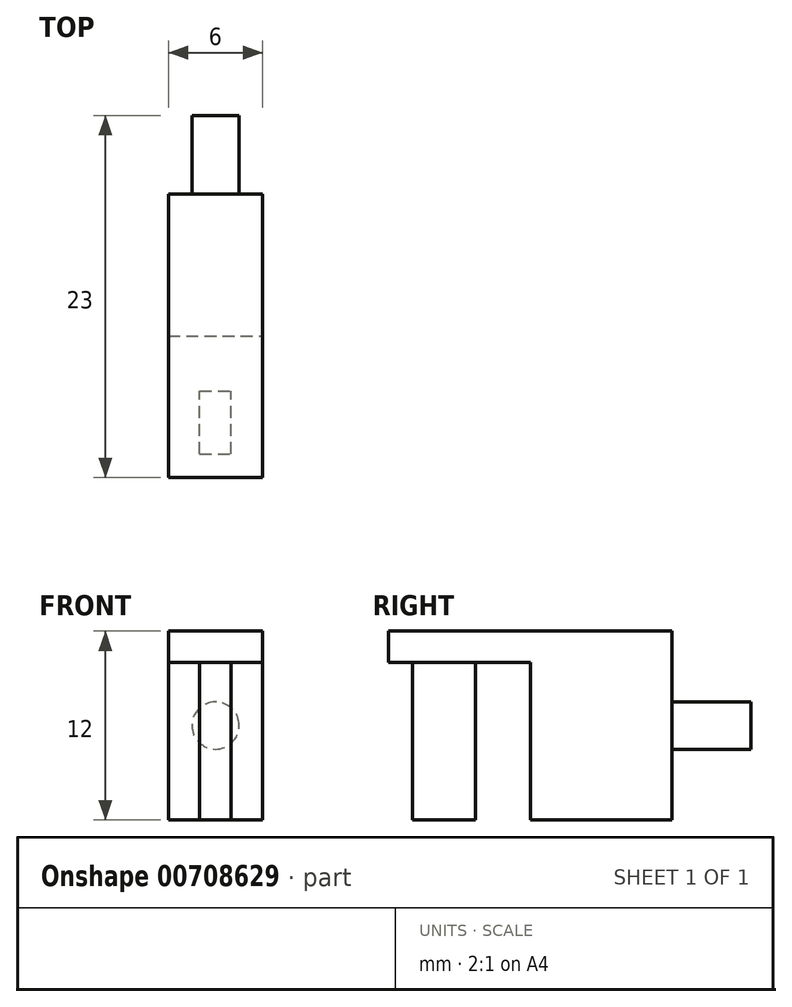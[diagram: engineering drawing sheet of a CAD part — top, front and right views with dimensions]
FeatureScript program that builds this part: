
annotation { "Feature Type Name" : "Feature", "Feature Type Description" : "" }
export const myFeature = defineFeature(function(context is Context, id is Id, definition is map)
    precondition{}
    {
        {
            var Q0;
            Q0=qCreatedBy(makeId("Top.planeOp"),FACE);
            var sketch = newSketch(context, id + "F0", { "sketchPlane" : qUnion([Q0])});
            skLineSegment(sketch, "E0.bottom", {"start": v(-3, 9) * mm, "end": v(3, 9) * mm});
            skLineSegment(sketch, "E0.top", {"start": v(-3, -9) * mm, "end": v(3, -9) * mm});
            skLineSegment(sketch, "E0.left", {"start": v(-3, 9) * mm, "end": v(-3, -9) * mm});
            skLineSegment(sketch, "E0.right", {"start": v(3, 9) * mm, "end": v(3, -9) * mm});
            skPoint(sketch, "E0.middle", {"position": v(0, 0) * mm});
            skSolve(sketch);
        }
        {
            var Q0;
            Q0=makeQuery(id+"F0.imprint","IMPRINT",FACE,{"disambiguationData":[TD([[makeQuery(id+"F0.imprint","IMPRINT",EDGE,{"derivedFrom":sQuery(id+"F0.wireOp",EDGE,"E0.bottom")}),-1.0]])]});
            extrude(context, id + "F1", {"entities" : qUnion([Q0]), "depth" : 12 * mm, "offsetDistance" : 25 * mm});
        }
        {
            var Q0;
            Q0=makeQuery(id+"F1.opExtrude","CAP_FACE",FACE,{"disambiguationData":[OSD([sQuery(id+"F0.wireOp",EDGE,"E0.bottom"),sQuery(id+"F0.wireOp",EDGE,"E0.top"),sQuery(id+"F0.wireOp",EDGE,"E0.left"),sQuery(id+"F0.wireOp",EDGE,"E0.right")])],"isStart":true});
            var sketch = newSketch(context, id + "F2", { "sketchPlane" : qUnion([Q0])});
            skLineSegment(sketch, "E1.bottom", {"start": v(-3, 9) * mm, "end": v(3, 9) * mm});
            skLineSegment(sketch, "E1.top", {"start": v(-3, 0) * mm, "end": v(3, 0) * mm});
            skLineSegment(sketch, "E1.left", {"start": v(-3, 9) * mm, "end": v(-3, 0) * mm});
            skLineSegment(sketch, "E1.right", {"start": v(3, 9) * mm, "end": v(3, 0) * mm});
            skLineSegment(sketch, "E2.bottom", {"start": v(-1, 7.5) * mm, "end": v(1, 7.5) * mm});
            skLineSegment(sketch, "E2.top", {"start": v(-1, 3.5) * mm, "end": v(1, 3.5) * mm});
            skLineSegment(sketch, "E2.left", {"start": v(-1, 7.5) * mm, "end": v(-1, 3.5) * mm});
            skLineSegment(sketch, "E2.right", {"start": v(1, 7.5) * mm, "end": v(1, 3.5) * mm});
            skPoint(sketch, "E2.middle", {"position": v(0, 5.5) * mm});
            skSolve(sketch);
        }
        {
            var Q0;
            Q0=makeQuery(id+"F2.imprint","IMPRINT",FACE,{"disambiguationData":[TD([[makeQuery(id+"F2.imprint","IMPRINT",EDGE,{"derivedFrom":sQuery(id+"F2.wireOp",EDGE,"E1.bottom")}),-1.0]])]});
            extrude(context, id + "F3", {"entities" : qUnion([Q0]), "operationType" : NewBodyOperationType.REMOVE, "oppositeDirection" : true, "depth" : 10 * mm, "offsetDistance" : 25 * mm});
        }
        {
            var Q0;
            Q0=makeQuery(id+"F1.opExtrude","SWEPT_FACE",FACE,{"disambiguationData":[OSD([sQuery(id+"F0.wireOp",EDGE,"E0.bottom")])]});
            var sketch = newSketch(context, id + "F4", { "sketchPlane" : qUnion([Q0])});
            skCircle(sketch, "E3", {"center": v(0, 6) * mm, "radius": 1.5 * mm});
            skSolve(sketch);
        }
        {
            var Q0;
            Q0=makeQuery(id+"F4.imprint","IMPRINT",FACE,{"disambiguationData":[TD([[makeQuery(id+"F4.imprint","IMPRINT",EDGE,{"derivedFrom":sQuery(id+"F4.wireOp",EDGE,"E3")}),1.0]])]});
            extrude(context, id + "F5", {"entities" : qUnion([Q0]), "operationType" : NewBodyOperationType.ADD, "depth" : 5 * mm, "offsetDistance" : 25 * mm});
        }
    });
